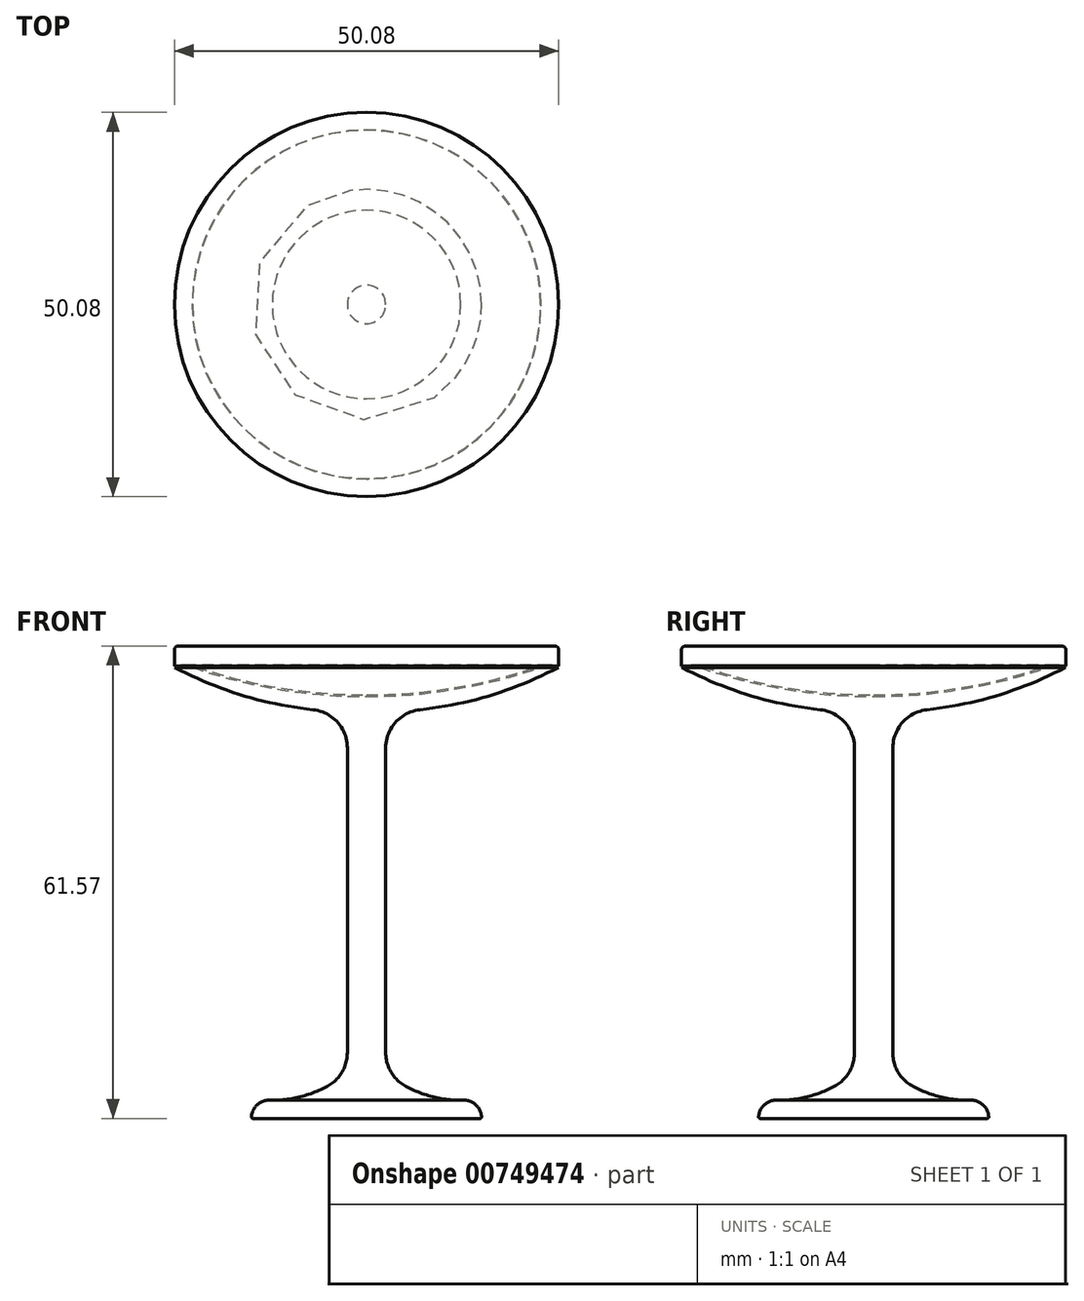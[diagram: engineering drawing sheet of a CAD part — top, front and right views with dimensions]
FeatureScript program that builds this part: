
annotation { "Feature Type Name" : "Feature", "Feature Type Description" : "" }
export const myFeature = defineFeature(function(context is Context, id is Id, definition is map)
    precondition{}
    {
        {
            var Q0;
            Q0=qCreatedBy(makeId("Front.planeOp"),FACE);
            var sketch = newSketch(context, id + "F0", { "sketchPlane" : qUnion([Q0])});
            skLineSegment(sketch, "E0", {"start": v(-15, 0) * mm, "end": v(0, 0) * mm});
            skLineSegment(sketch, "E1", {"start": v(0, 0) * mm, "end": v(0, 53) * mm});
            skLineSegment(sketch, "E2", {"start": v(-2.5, 5.94) * mm, "end": v(-2.5, 53) * mm});
            skArc(sketch, "E3", {"start": v(-25, 58.8) * mm, "mid": v(-14.1, 54.57) * mm, "end": v(-2.5, 53) * mm});
            skArc(sketch, "E4", {"start": v(-22.74, 58.82) * mm, "mid": v(-23.87, 58.87) * mm, "end": v(-25, 58.8) * mm});
            skArc(sketch, "E5", {"start": v(-22.74, 58.82) * mm, "mid": v(-11.53, 55.96) * mm, "end": v(0, 55) * mm});
            skArc(sketch, "E6", {"start": v(-12.29, 2.35) * mm, "mid": v(-7.09, 3.3) * mm, "end": v(-2.5, 5.94) * mm});
            skArc(sketch, "E7", {"start": v(-12.29, 2.35) * mm, "mid": v(-14.2, 1.81) * mm, "end": v(-15, 0) * mm});
            skLineSegment(sketch, "E8", {"start": v(0, 55) * mm, "end": v(9.32, 55) * mm, "construction": true});
            skLineSegment(sketch, "E9", {"start": v(0, 53) * mm, "end": v(0, 55) * mm});
            skLineSegment(sketch, "E10", {"start": v(-25.04, 61.57) * mm, "end": v(0, 61.57) * mm});
            skArc(sketch, "E11.0", {"start": v(-22.7, 59.01) * mm, "mid": v(-11.5, 56.16) * mm, "end": v(0, 55.2) * mm});
            skArc(sketch, "E11.1", {"start": v(-22.7, 59.01) * mm, "mid": v(-23.87, 59.07) * mm, "end": v(-25.04, 59) * mm});
            skLineSegment(sketch, "E12", {"start": v(-25.04, 61.57) * mm, "end": v(-25.04, 59) * mm});
            skLineSegment(sketch, "E13", {"start": v(0, 61.57) * mm, "end": v(0, 55.2) * mm});
            skSolve(sketch);
        }
        {
            var Q0;
            Q0 = qSketchRegion(id + "F0", true);
            var Q1;
            Q1=sQuery(id+"F0.wireOp",EDGE,"E1");
            revolve(context, id + "F1", {"surfaceOperationType" : NewSurfaceOperationType.NEW, "entities" : qUnion([Q0]), "axis" : qUnion([Q1]), "revolveType" : RevolveType.FULL});
        }
        {
            var Q0;
            Q0=makeQuery(id+"F1.opRevolve","SWEPT_EDGE",EDGE,{"disambiguationData":[OSD([sQuery(id+"F0.wireOp",EDGE,"E10"),sQuery(id+"F0.wireOp",EDGE,"E12")])]});
            fillet(context, id + "F2", {"entities" : qUnion([Q0]), "radius" : .5 * mm, "tangentPropagation" : true, "allowEdgeOverflow" : false});
        }
        {
            var Q0;
            Q0=makeQuery(id+"F1.opRevolve","SWEPT_EDGE",EDGE,{"disambiguationData":[OSD([sQuery(id+"F0.wireOp",EDGE,"E2"),sQuery(id+"F0.wireOp",EDGE,"E6")])]});
            fillet(context, id + "F3", {"entities" : qUnion([Q0]), "radius" : 5 * mm, "tangentPropagation" : true, "allowEdgeOverflow" : false});
        }
        {
            var Q0;
            Q0=makeQuery(id+"F1.opRevolve","SWEPT_EDGE",EDGE,{"disambiguationData":[OSD([sQuery(id+"F0.wireOp",EDGE,"E0"),sQuery(id+"F0.wireOp",EDGE,"E7")])]});
            fillet(context, id + "F4", {"entities" : qUnion([Q0]), "radius" : .2 * mm, "tangentPropagation" : true, "allowEdgeOverflow" : false});
        }
        {
            var Q0;
            Q0=makeQuery(id+"F1.opRevolve","SWEPT_EDGE",EDGE,{"disambiguationData":[OSD([sQuery(id+"F0.wireOp",EDGE,"E2"),sQuery(id+"F0.wireOp",EDGE,"E3")])]});
            fillet(context, id + "F5", {"entities" : qUnion([Q0]), "radius" : 5 * mm, "tangentPropagation" : true, "allowEdgeOverflow" : false});
        }
    });
